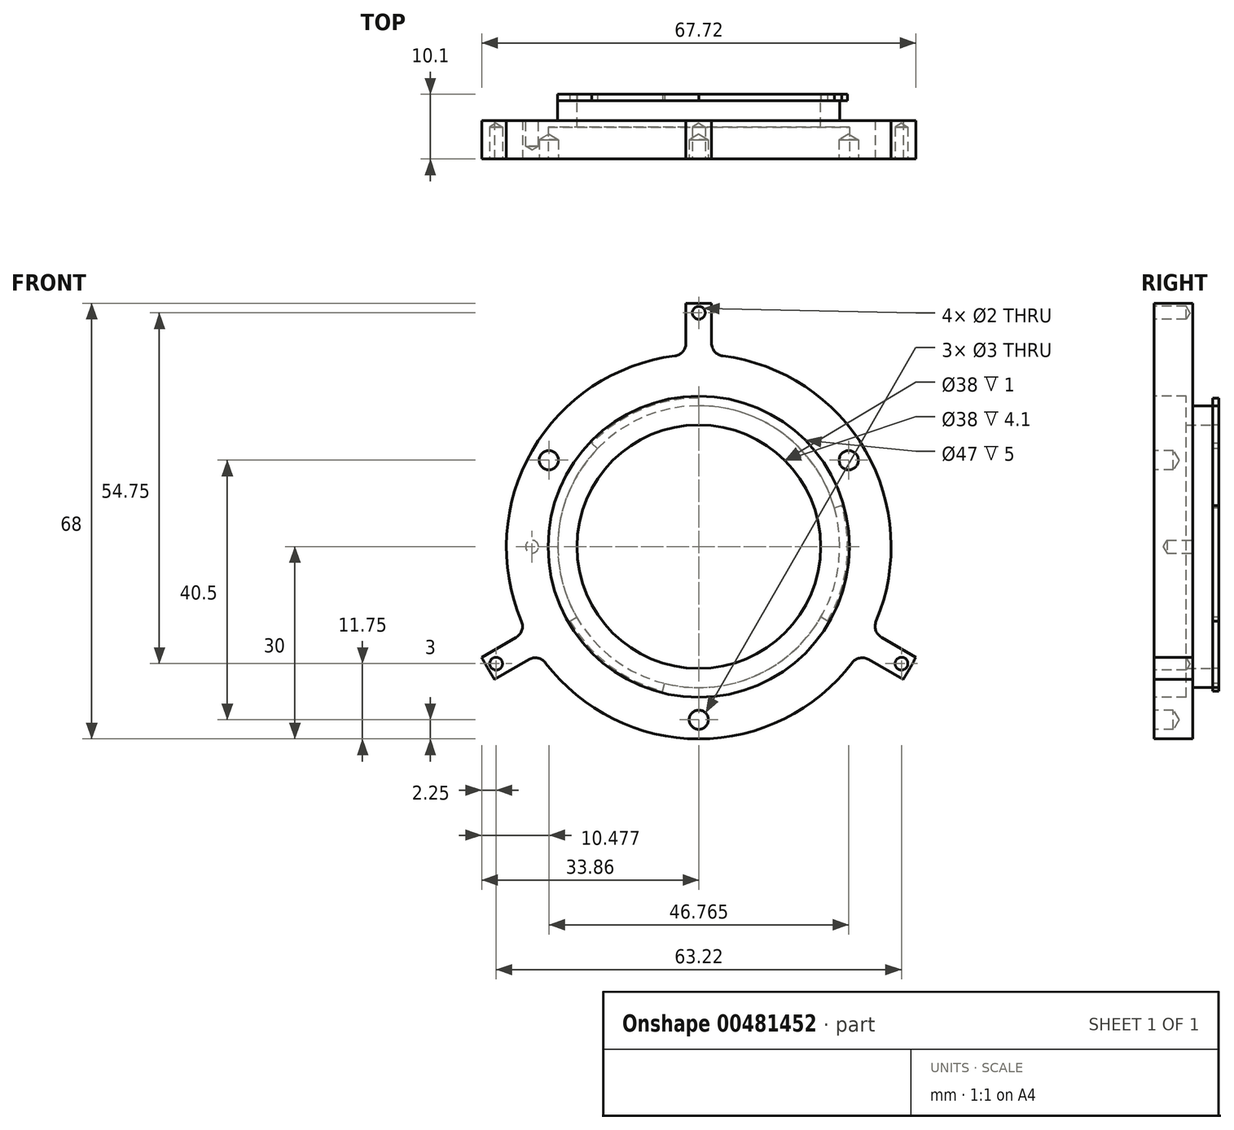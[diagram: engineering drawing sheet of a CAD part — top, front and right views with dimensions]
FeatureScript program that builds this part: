
annotation { "Feature Type Name" : "Feature", "Feature Type Description" : "" }
export const myFeature = defineFeature(function(context is Context, id is Id, definition is map)
    precondition{}
    {
        {
            var Q0;
            Q0=qCreatedBy(makeId("Front.planeOp"),FACE);
            var sketch = newSketch(context, id + "F0", { "sketchPlane" : qUnion([Q0])});
            skCircle(sketch, "E0", {"center": v(0, 0) * mm, "radius": 38 * mm});
            skCircle(sketch, "E1", {"center": v(0, 0) * mm, "radius": 19 * mm});
            skSolve(sketch);
        }
        {
            var Q0;
            Q0 = qSketchRegion(id + "F0", true);
            extrude(context, id + "F1", {"entities" : qUnion([Q0]), "depth" : 6 * mm});
        }
        {
            var Q0;
            Q0=makeQuery(id+"F1.opExtrude","CAP_FACE",FACE,{"disambiguationData":[OSD([sQuery(id+"F0.wireOp",EDGE,"E0"),sQuery(id+"F0.wireOp",EDGE,"E1")])],"isStart":true});
            var sketch = newSketch(context, id + "F2", { "sketchPlane" : qUnion([Q0])});
            skCircle(sketch, "E2", {"center": v(0, 0) * mm, "radius": 22 * mm});
            skCircle(sketch, "E3", {"center": v(0, 0) * mm, "radius": 19 * mm});
            skSolve(sketch);
        }
        {
            var Q0;
            Q0 = qSketchRegion(id + "F2", true);
            extrude(context, id + "F3", {"entities" : qUnion([Q0]), "operationType" : NewBodyOperationType.ADD, "depth" : 3.1 * mm});
        }
        {
            var Q0;
            Q0=makeQuery(id+"F3.opExtrude","CAP_FACE",FACE,{"disambiguationData":[OSD([sQuery(id+"F2.wireOp",EDGE,"E2"),sQuery(id+"F2.wireOp",EDGE,"E3")])],"isStart":false});
            var sketch = newSketch(context, id + "F4", { "sketchPlane" : qUnion([Q0])});
            skArc(sketch, "E4", {"start": v(-22.3, 6.4) * mm, "mid": v(-23.03, -2.83) * mm, "end": v(-20.1, -11.6) * mm});
            skArc(sketch, "E5", {"start": v(0, 22) * mm, "mid": v(-13.24, 17.57) * mm, "end": v(-21.15, 6.06) * mm});
            skCircle(sketch, "E6", {"center": v(0, 0) * mm, "radius": 19 * mm});
            skLineSegment(sketch, "E7", {"start": v(-22.3, 6.4) * mm, "end": v(-21.15, 6.06) * mm});
            skLineSegment(sketch, "E8", {"start": v(-20.1, -11.6) * mm, "end": v(-19.05, -11) * mm});
            skLineSegment(sketch, "E9", {"start": v(5.61, -22.51) * mm, "end": v(5.32, -21.35) * mm});
            skLineSegment(sketch, "E10", {"start": v(20.1, -11.6) * mm, "end": v(19.05, -11) * mm});
            skLineSegment(sketch, "E11.trimOffspring", {"start": v(0, 22) * mm, "end": v(0, 23.2) * mm});
            skLineSegment(sketch, "E12.trimOffspring", {"start": v(15.83, 15.28) * mm, "end": v(16.69, 16.12) * mm});
            skArc(sketch, "E13.trimOffspring", {"start": v(-19.05, -11) * mm, "mid": v(-8.6, -20.25) * mm, "end": v(5.32, -21.35) * mm});
            skArc(sketch, "E14.trimOffspring", {"start": v(19.05, -11) * mm, "mid": v(21.84, 2.68) * mm, "end": v(15.83, 15.28) * mm});
            skArc(sketch, "E15.trimOffspring", {"start": v(16.69, 16.12) * mm, "mid": v(9.06, 21.36) * mm, "end": v(0, 23.2) * mm});
            skArc(sketch, "E16.trimOffspring", {"start": v(5.61, -22.51) * mm, "mid": v(13.96, -18.53) * mm, "end": v(20.1, -11.6) * mm});
            skSolve(sketch);
        }
        {
            var Q0;
            Q0 = qSketchRegion(id + "F4", true);
            var Q1;
            Q1=sQuery(id+"F4.wireOp",EDGE,"35ZCHtBD-Pb0S-crrr-TfdC-wMtguIC25ghE");
            var Q2;
            Q2=sQuery(id+"F4.wireOp",EDGE,"pjZac7zb-o6VC-IGMA-mHPJ-N6sJrFxxSYox");
            var Q3;
            Q3=sQuery(id+"F4.wireOp",EDGE,"vGOVhm5Q-oqCW-BzUn-e2tP-DzXSbPJOlnTf");
            var Q4;
            Q4=sQuery(id+"F4.wireOp",EDGE,"M5Pvd3Os-9wTu-yBbd-SL1T-Nv6YX8CQMhYz");
            var Q5;
            Q5=sQuery(id+"F4.wireOp",EDGE,"47cf342f-56c0-46b6-b771-fd9bc8488513.trimOffspring");
            var Q6;
            Q6=sQuery(id+"F4.wireOp",EDGE,"fOVqg1Zd-seWb-Ob9E-AZis-hUE17Vxpxq3d");
            extrude(context, id + "F5", {"entities" : qUnion([Q0]), "surfaceEntities" : qUnion([Q1, Q2, Q3, Q4, Q5, Q6]), "depth" : 1 * mm});
        }
        {
            var Q0;
            Q0=makeQuery(id+"F1.opExtrude","CAP_FACE",FACE,{"disambiguationData":[OSD([sQuery(id+"F0.wireOp",EDGE,"E0"),sQuery(id+"F0.wireOp",EDGE,"E1")])],"isStart":true});
            var sketch = newSketch(context, id + "F6", { "sketchPlane" : qUnion([Q0])});
            skPoint(sketch, "E17", {"position": v(26, 0) * mm});
            skSolve(sketch);
        }
        {
            var Q0;
            Q0=sQuery(id+"F6.wireOp",VERTEX,"E17");
            var Q1;
            Q1=makeQuery(id+"F1.opExtrude","SWEPT_BODY",BODY,{"disambiguationData":[OSD([sQuery(id+"F0.wireOp",EDGE,"E0"),sQuery(id+"F0.wireOp",EDGE,"E1")])]});
            hole(context, id + "F7", {"style" : HoleStyle.SIMPLE, "endStyle" : HoleEndStyle.BLIND, "holeDiameter" : 2 * mm, "holeDepth" : 4 * mm, "isTappedThrough" : true, "tappedDepth" : 12 * mm, "tapClearance" : 3, "locations" : qUnion([Q0]), "scope" : qUnion([Q1])});
        }
        {
            var Q0;
            Q0=makeQuery(id+"F1.opExtrude","CAP_FACE",FACE,{"disambiguationData":[OSD([sQuery(id+"F0.wireOp",EDGE,"E0"),sQuery(id+"F0.wireOp",EDGE,"E1")])],"isStart":false});
            var sketch = newSketch(context, id + "F8", { "sketchPlane" : qUnion([Q0])});
            skPoint(sketch, "E18", {"position": v(23.38, 13.5) * mm});
            skLineSegment(sketch, "E19", {"start": v(0, 0) * mm, "end": v(35.09, 20.26) * mm, "construction": true});
            skLineSegment(sketch, "E20", {"start": v(0, 0) * mm, "end": v(-35.23, 20.34) * mm, "construction": true});
            skLineSegment(sketch, "E21", {"start": v(0, 0) * mm, "end": v(0, -41.92) * mm, "construction": true});
            skLineSegment(sketch, "E22", {"start": v(0, 0) * mm, "end": v(-35.01, -20.21) * mm, "construction": true});
            skLineSegment(sketch, "E23", {"start": v(0, 0) * mm, "end": v(34, -19.63) * mm, "construction": true});
            skLineSegment(sketch, "E24", {"start": v(0, 0) * mm, "end": v(0, 41.54) * mm, "construction": true});
            skCircle(sketch, "E25", {"center": v(0, 0) * mm, "radius": 27 * mm, "construction": true});
            skPoint(sketch, "E26", {"position": v(-23.38, 13.5) * mm});
            skPoint(sketch, "E27", {"position": v(-31.6, -18.25) * mm});
            skPoint(sketch, "E28", {"position": v(0, -27) * mm});
            skPoint(sketch, "E29", {"position": v(31.6, -18.25) * mm});
            skCircle(sketch, "E30", {"center": v(0, 0) * mm, "radius": 36.5 * mm, "construction": true});
            skPoint(sketch, "E31", {"position": v(0, 36.5) * mm});
            skSolve(sketch);
        }
        {
            var Q0;
            Q0=sQuery(id+"F8.wireOp",VERTEX,"E18");
            var Q1;
            Q1=sQuery(id+"F8.wireOp",VERTEX,"E26");
            var Q2;
            Q2=sQuery(id+"F8.wireOp",VERTEX,"E28");
            var Q3;
            Q3=makeQuery(id+"F1.opExtrude","SWEPT_BODY",BODY,{"disambiguationData":[OSD([sQuery(id+"F0.wireOp",EDGE,"E0"),sQuery(id+"F0.wireOp",EDGE,"E1")])]});
            hole(context, id + "F9", {"style" : HoleStyle.SIMPLE, "endStyle" : HoleEndStyle.BLIND, "holeDiameter" : 3 * mm, "holeDepth" : 3 * mm, "isTappedThrough" : true, "tappedDepth" : 12 * mm, "tapClearance" : 3, "locations" : qUnion([Q0, Q1, Q2]), "scope" : qUnion([Q3])});
        }
        {
            var Q0;
            Q0=sQuery(id+"F8.wireOp",VERTEX,"E31");
            var Q1;
            Q1=sQuery(id+"F8.wireOp",VERTEX,"E29");
            var Q2;
            Q2=sQuery(id+"F8.wireOp",VERTEX,"E27");
            var Q3;
            Q3=makeQuery(id+"F1.opExtrude","SWEPT_BODY",BODY,{"disambiguationData":[OSD([sQuery(id+"F0.wireOp",EDGE,"E0"),sQuery(id+"F0.wireOp",EDGE,"E1")])]});
            hole(context, id + "F10", {"style" : HoleStyle.SIMPLE, "endStyle" : HoleEndStyle.BLIND, "holeDiameter" : 2 * mm, "holeDepth" : 5 * mm, "isTappedThrough" : true, "tappedDepth" : 12 * mm, "tapClearance" : 3, "locations" : qUnion([Q0, Q1, Q2]), "scope" : qUnion([Q3])});
        }
        {
            var Q0;
            Q0=makeQuery(id+"F8.imprint","IMPRINT",FACE,{"disambiguationData":[TD([[makeQuery(id+"F8.imprint","IMPRINT",EDGE,{"derivedFrom":makeQuery(id+"F1.opExtrude","CAP_EDGE",EDGE,{"disambiguationData":[OSD([sQuery(id+"F0.wireOp",EDGE,"E0")])],"isStart":false})}),1.0]])]});
            var sketch = newSketch(context, id + "F11", { "sketchPlane" : qUnion([Q0])});
            skArc(sketch, "E32", {"start": v(-3.75, 29.76) * mm, "mid": v(-25.98, 15) * mm, "end": v(-27.65, -11.63) * mm});
            skLineSegment(sketch, "E33.bottom", {"start": v(31.86, -20.7) * mm, "end": v(26.5, -17.6) * mm});
            skLineSegment(sketch, "E33.top", {"start": v(33.86, -17.24) * mm, "end": v(28.5, -14.14) * mm});
            skLineSegment(sketch, "E34.bottom", {"start": v(2, 37.95) * mm, "end": v(2, 31.75) * mm});
            skLineSegment(sketch, "E34.top", {"start": v(-2, 37.95) * mm, "end": v(-2, 31.75) * mm});
            skArc(sketch, "E35", {"start": v(31.86, -20.7) * mm, "mid": v(32.9, -19) * mm, "end": v(33.86, -17.24) * mm});
            skArc(sketch, "E36.trimOffspring", {"start": v(27.65, -11.63) * mm, "mid": v(25.98, 15) * mm, "end": v(3.75, 29.76) * mm});
            skArc(sketch, "E37.trimOffspring", {"start": v(-23.9, -18.13) * mm, "mid": v(0, -30) * mm, "end": v(23.9, -18.13) * mm});
            skLineSegment(sketch, "E38.trimOffspring", {"start": v(-26.5, -17.6) * mm, "end": v(-31.86, -20.7) * mm});
            skLineSegment(sketch, "E39.trimOffspring", {"start": v(-28.5, -14.14) * mm, "end": v(-33.86, -17.24) * mm});
            skPoint(sketch, "E40.orphan", {"position": v(2.5, -4.33) * mm});
            skPoint(sketch, "E41.orphan", {"position": v(-1, -1.73) * mm});
            skPoint(sketch, "E33.right.end.orphan", {"position": v(1, 1.73) * mm});
            skPoint(sketch, "E42.top.start.orphan", {"position": v(-2.5, 4.33) * mm});
            skPoint(sketch, "E43.orphan", {"position": v(-2, 0) * mm});
            skPoint(sketch, "E44.orphan", {"position": v(2, 0) * mm});
            skPoint(sketch, "E45.visualSharp", {"position": v(26.92, -13.23) * mm});
            skArc(sketch, "E45.filletArc", {"start": v(27.65, -11.63) * mm, "mid": v(27.6, -13.05) * mm, "end": v(28.5, -14.14) * mm});
            skPoint(sketch, "E46.visualSharp", {"position": v(24.92, -16.7) * mm});
            skArc(sketch, "E46.filletArc", {"start": v(26.5, -17.6) * mm, "mid": v(25.1, -17.38) * mm, "end": v(23.9, -18.13) * mm});
            skPoint(sketch, "E47.visualSharp", {"position": v(-24.92, -16.7) * mm});
            skArc(sketch, "E47.filletArc", {"start": v(-23.9, -18.13) * mm, "mid": v(-25.1, -17.38) * mm, "end": v(-26.5, -17.6) * mm});
            skPoint(sketch, "E48.visualSharp", {"position": v(-26.92, -13.23) * mm});
            skArc(sketch, "E48.filletArc", {"start": v(-28.5, -14.14) * mm, "mid": v(-27.6, -13.05) * mm, "end": v(-27.65, -11.63) * mm});
            skPoint(sketch, "E49.visualSharp", {"position": v(-2, 29.93) * mm});
            skArc(sketch, "E49.filletArc", {"start": v(-3.75, 29.76) * mm, "mid": v(-2.5, 30.43) * mm, "end": v(-2, 31.75) * mm});
            skPoint(sketch, "E50.visualSharp", {"position": v(2, 29.93) * mm});
            skArc(sketch, "E50.filletArc", {"start": v(2, 31.75) * mm, "mid": v(2.5, 30.43) * mm, "end": v(3.75, 29.76) * mm});
            skArc(sketch, "E51.trimOffspring", {"start": v(2, 37.95) * mm, "mid": v(0, 38) * mm, "end": v(-2, 37.95) * mm});
            skArc(sketch, "E52.trimOffspring", {"start": v(-33.86, -17.24) * mm, "mid": v(-32.9, -19) * mm, "end": v(-31.86, -20.7) * mm});
            skSolve(sketch);
        }
        {
            var Q0;
            Q0 = qSketchRegion(id + "F11", true);
            extrude(context, id + "F12", {"entities" : qUnion([Q0]), "operationType" : NewBodyOperationType.INTERSECT, "endBound" : BoundingType.THROUGH_ALL, "oppositeDirection" : true, "depth" : 25 * mm});
        }
        {
            var Q0;
            Q0=makeQuery(id+"F8.imprint","IMPRINT",FACE,{"disambiguationData":[TD([[makeQuery(id+"F8.imprint","IMPRINT",EDGE,{"derivedFrom":makeQuery(id+"F1.opExtrude","CAP_EDGE",EDGE,{"disambiguationData":[OSD([sQuery(id+"F0.wireOp",EDGE,"E0")])],"isStart":false})}),1.0]])]});
            var sketch = newSketch(context, id + "F13", { "sketchPlane" : qUnion([Q0])});
            skCircle(sketch, "E53", {"center": v(0, 0) * mm, "radius": 23.5 * mm});
            skSolve(sketch);
        }
        {
            var Q0;
            Q0 = qSketchRegion(id + "F13", true);
            extrude(context, id + "F14", {"entities" : qUnion([Q0]), "operationType" : NewBodyOperationType.REMOVE, "oppositeDirection" : true, "depth" : 5 * mm, "offsetDistance" : 25 * mm});
        }
    });
